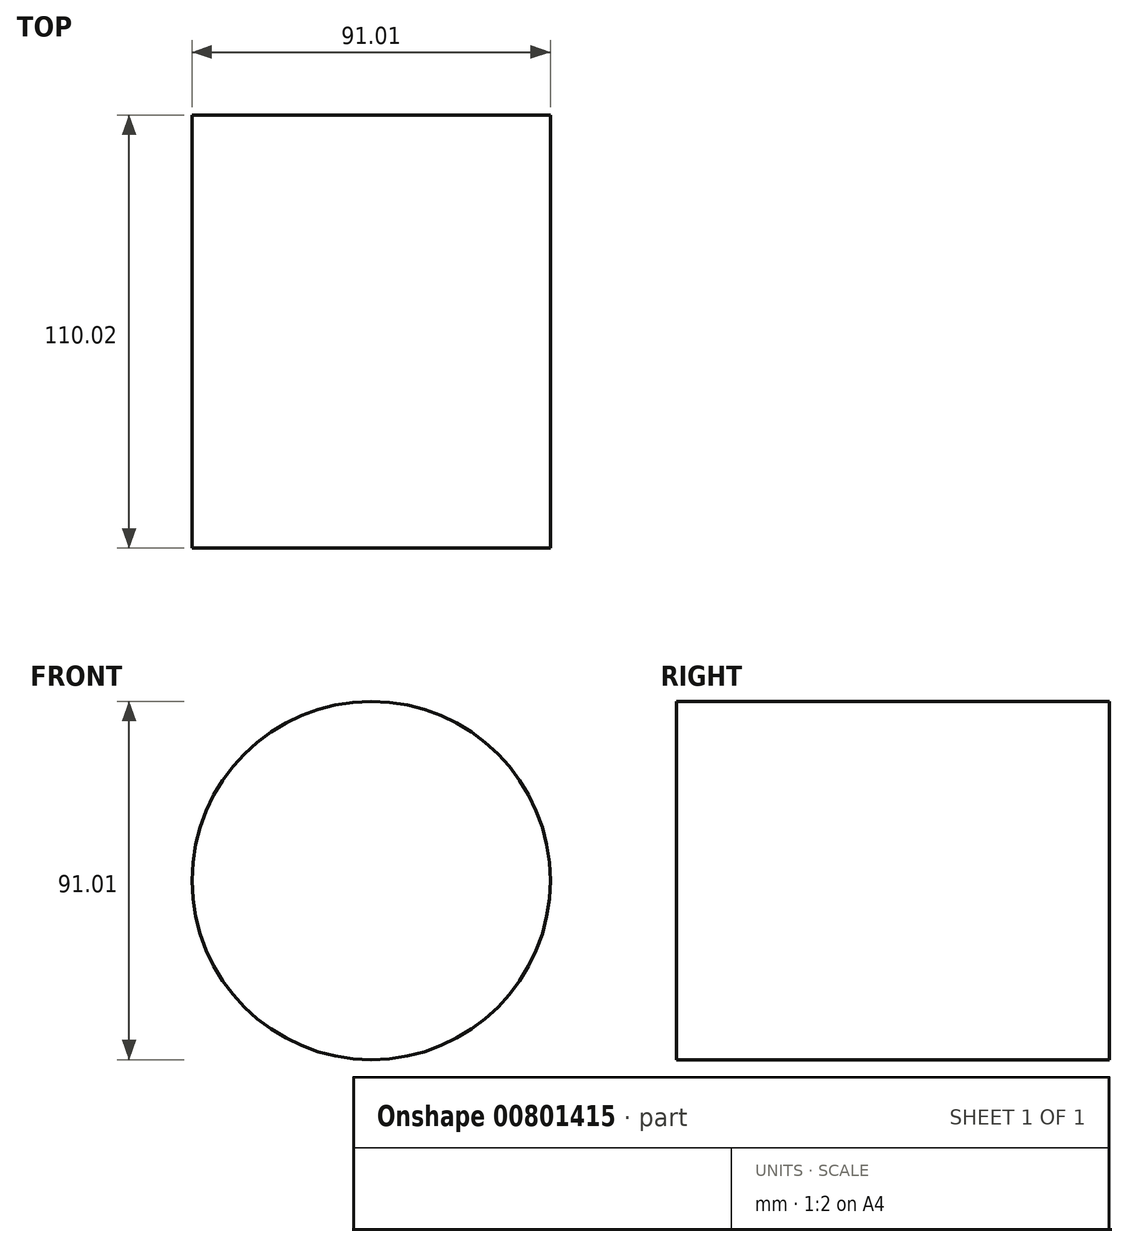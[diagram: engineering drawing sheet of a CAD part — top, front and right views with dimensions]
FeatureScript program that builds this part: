
annotation { "Feature Type Name" : "Feature", "Feature Type Description" : "" }
export const myFeature = defineFeature(function(context is Context, id is Id, definition is map)
    precondition{}
    {
        {
            var Q0;
            Q0=qCreatedBy(makeId("Top.planeOp"),FACE);
            var sketch = newSketch(context, id + "F0", { "sketchPlane" : qUnion([Q0])});
            skCircle(sketch, "E0", {"center": v(0, 0) * mm, "radius": 50.62 * mm});
            skSolve(sketch);
        }
        {
            var Q0;
            Q0=sQuery(id+"F0.wireOp",EDGE,"E0");
            extrude(context, id + "F1", {"bodyType" : ToolBodyType.SURFACE, "surfaceEntities" : qUnion([Q0]), "depth" : 43.74 * mm, "offsetDistance" : 25 * mm});
        }
        {
            var Q0;
            Q0=qCreatedBy(makeId("Front.planeOp"),FACE);
            var sketch = newSketch(context, id + "F2", { "sketchPlane" : qUnion([Q0])});
            skCircle(sketch, "E1", {"center": v(-61.12, 65.27) * mm, "radius": 45.5 * mm});
            skSolve(sketch);
        }
        {
            var Q0;
            Q0=makeQuery(id+"F2.imprint","IMPRINT",FACE,{"disambiguationData":[TD([[makeQuery(id+"F2.imprint","IMPRINT",EDGE,{"derivedFrom":sQuery(id+"F2.wireOp",EDGE,"E1")}),1.0]])]});
            extrude(context, id + "F3", {"entities" : qUnion([Q0]), "depth" : 110.02 * mm, "offsetDistance" : 25 * mm});
        }
    });
